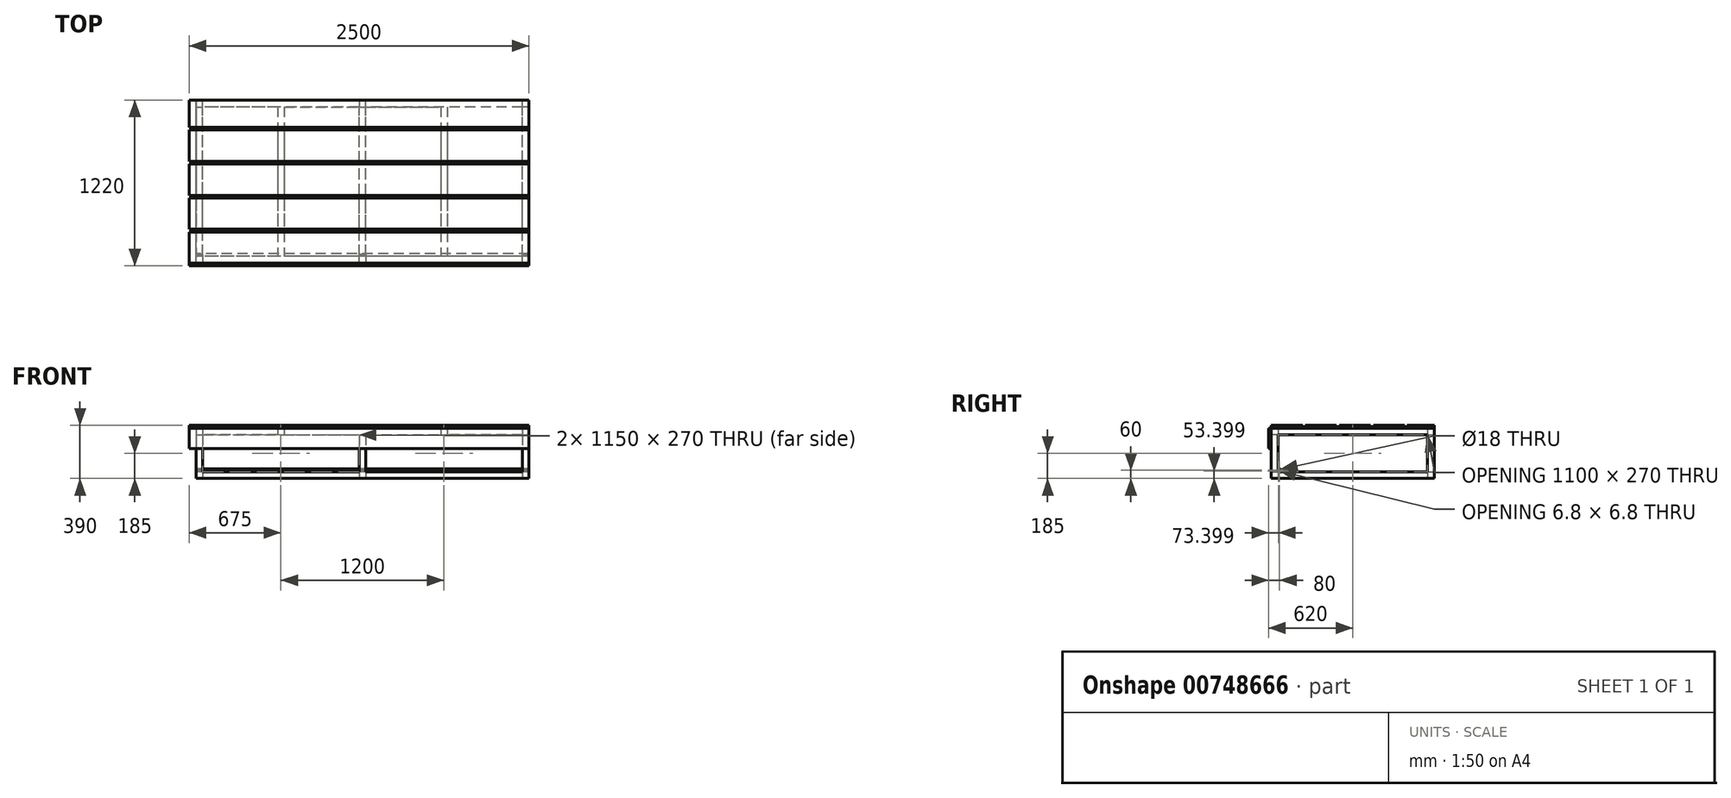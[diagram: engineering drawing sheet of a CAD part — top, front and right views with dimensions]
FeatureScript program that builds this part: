
annotation { "Feature Type Name" : "Feature", "Feature Type Description" : "" }
export const myFeature = defineFeature(function(context is Context, id is Id, definition is map)
    precondition{}
    {
        {
            var Q0;
            Q0=qCreatedBy(makeId("Top.planeOp"),FACE);
            var sketch = newSketch(context, id + "F0", { "sketchPlane" : qUnion([Q0])});
            skLineSegment(sketch, "E0.bottom", {"start": v(1225, -600) * mm, "end": v(-1225, -600) * mm});
            skLineSegment(sketch, "E0.top", {"start": v(1225, 600) * mm, "end": v(-1225, 600) * mm});
            skLineSegment(sketch, "E0.left", {"start": v(1225, -600) * mm, "end": v(1225, 600) * mm});
            skLineSegment(sketch, "E0.right", {"start": v(-1225, -600) * mm, "end": v(-1225, 600) * mm});
            skPoint(sketch, "E0.middle", {"position": v(0, 0) * mm});
            skLineSegment(sketch, "E1.0", {"start": v(1225, 550) * mm, "end": v(-1225, 550) * mm});
            skLineSegment(sketch, "E2.0", {"start": v(1227.5, -600) * mm, "end": v(1227.5, 600) * mm});
            skLineSegment(sketch, "E3.0", {"start": v(1175, -600) * mm, "end": v(1175, 600) * mm});
            skLineSegment(sketch, "E4.0", {"start": v(1225, -550) * mm, "end": v(-1225, -550) * mm});
            skLineSegment(sketch, "E5.0", {"start": v(-1175, -600) * mm, "end": v(-1175, 600) * mm});
            skLineSegment(sketch, "E6", {"start": v(0, 0) * mm, "end": v(0, 550) * mm});
            skLineSegment(sketch, "E7", {"start": v(0, 0) * mm, "end": v(0, -550) * mm});
            skLineSegment(sketch, "E8.0", {"start": v(25, 0) * mm, "end": v(25, 550) * mm});
            skLineSegment(sketch, "E9.0", {"start": v(-25, 0) * mm, "end": v(-25, 550) * mm});
            skLineSegment(sketch, "E10.0", {"start": v(-25, 0) * mm, "end": v(-25, -550) * mm});
            skLineSegment(sketch, "E11.0", {"start": v(25, 0) * mm, "end": v(25, -550) * mm});
            skSolve(sketch);
        }
        {
            var Q0;
            Q0 = qSketchRegion(id + "F0", true);
            var Q1;
            {var subQ1=sQuery(id+"F0.wireOp",EDGE,"E6");Q1=makeQuery(id+"F0.imprint","IMPRINT",FACE,{"disambiguationData":[TD([[makeQuery(id+"F0.imprint","IMPRINT",EDGE,{"derivedFrom":subQ1}),-1.0]])]});}
            var Q2;
            {var subQ3=sQuery(id+"F0.wireOp",EDGE,"E6");Q2=makeQuery(id+"F0.imprint","IMPRINT",FACE,{"disambiguationData":[TD([[makeQuery(id+"F0.imprint","IMPRINT",EDGE,{"derivedFrom":subQ3}),1.0]])]});}
            extrude(context, id + "F1", {"entities" : qUnion([Q0, Q1, Q2]), "depth" : 50 * mm, "offsetDistance" : 25 * mm});
        }
        {
            var Q0;
            Q0=makeQuery(id+"F1.opExtrude","CAP_FACE",FACE,{"disambiguationData":[OSD([sQuery(id+"F0.wireOp",EDGE,"E0.bottom"),sQuery(id+"F0.wireOp",EDGE,"E0.top"),sQuery(id+"F0.wireOp",EDGE,"E0.left"),sQuery(id+"F0.wireOp",EDGE,"E0.right"),sQuery(id+"F0.wireOp",EDGE,"E1.0"),sQuery(id+"F0.wireOp",EDGE,"E3.0"),sQuery(id+"F0.wireOp",EDGE,"E4.0"),sQuery(id+"F0.wireOp",EDGE,"E5.0"),sQuery(id+"F0.wireOp",EDGE,"E8.0"),sQuery(id+"F0.wireOp",EDGE,"E9.0"),sQuery(id+"F0.wireOp",EDGE,"E10.0"),sQuery(id+"F0.wireOp",EDGE,"E11.0")])],"isStart":false});
            var sketch = newSketch(context, id + "F2", { "sketchPlane" : qUnion([Q0])});
            skLineSegment(sketch, "E12", {"start": v(-25, 550) * mm, "end": v(25, 550) * mm});
            skLineSegment(sketch, "E13", {"start": v(25, 550) * mm, "end": v(25, 600) * mm});
            skLineSegment(sketch, "E14", {"start": v(25, 600) * mm, "end": v(-25, 600) * mm});
            skLineSegment(sketch, "E15", {"start": v(-25, 600) * mm, "end": v(-25, 550) * mm});
            skLineSegment(sketch, "E16", {"start": v(-1175, 550) * mm, "end": v(-1175, 600) * mm});
            skLineSegment(sketch, "E17", {"start": v(-1175, 600) * mm, "end": v(-1225, 600) * mm});
            skLineSegment(sketch, "E18", {"start": v(-1225, 600) * mm, "end": v(-1225, 550) * mm});
            skLineSegment(sketch, "E19", {"start": v(-1225, 550) * mm, "end": v(-1175, 550) * mm});
            skLineSegment(sketch, "E20", {"start": v(-1175, -550) * mm, "end": v(-1175, -600) * mm});
            skLineSegment(sketch, "E21", {"start": v(-1175, -600) * mm, "end": v(-1225, -600) * mm});
            skLineSegment(sketch, "E22", {"start": v(-1225, -600) * mm, "end": v(-1225, -550) * mm});
            skLineSegment(sketch, "E23", {"start": v(-1225, -550) * mm, "end": v(-1175, -550) * mm});
            skLineSegment(sketch, "E24", {"start": v(-25, -550) * mm, "end": v(25, -550) * mm});
            skLineSegment(sketch, "E25", {"start": v(25, -550) * mm, "end": v(25, -600) * mm});
            skLineSegment(sketch, "E26", {"start": v(25, -600) * mm, "end": v(-25, -600) * mm});
            skPoint(sketch, "E26.endSnap0", {"position": v(0, -600) * mm});
            skLineSegment(sketch, "E27", {"start": v(-25, -600) * mm, "end": v(-25, -550) * mm});
            skLineSegment(sketch, "E28", {"start": v(1175, -550) * mm, "end": v(1225, -550) * mm});
            skLineSegment(sketch, "E29", {"start": v(1225, -550) * mm, "end": v(1225, -600) * mm});
            skLineSegment(sketch, "E30", {"start": v(1225, -600) * mm, "end": v(1175, -600) * mm});
            skLineSegment(sketch, "E31", {"start": v(1175, -600) * mm, "end": v(1175, -550) * mm});
            skLineSegment(sketch, "E32", {"start": v(1175, 550) * mm, "end": v(1175, 600) * mm});
            skLineSegment(sketch, "E33", {"start": v(1175, 600) * mm, "end": v(1225, 600) * mm});
            skLineSegment(sketch, "E34", {"start": v(1225, 600) * mm, "end": v(1225, 550) * mm});
            skLineSegment(sketch, "E35", {"start": v(1225, 550) * mm, "end": v(1175, 550) * mm});
            skSolve(sketch);
        }
        {
            var Q0;
            Q0 = qSketchRegion(id + "F2", true);
            extrude(context, id + "F3", {"entities" : qUnion([Q0]), "operationType" : NewBodyOperationType.ADD, "depth" : 270 * mm, "offsetDistance" : 25 * mm});
        }
        {
            var Q0;
            Q0=makeQuery(id+"F3.opExtrude","CAP_FACE",FACE,{"disambiguationData":[OSD([sQuery(id+"F2.wireOp",EDGE,"E12"),sQuery(id+"F2.wireOp",EDGE,"E13"),sQuery(id+"F2.wireOp",EDGE,"E14"),sQuery(id+"F2.wireOp",EDGE,"E15")])],"isStart":false});
            var sketch = newSketch(context, id + "F4", { "sketchPlane" : qUnion([Q0])});
            skLineSegment(sketch, "E36.bottom", {"start": v(-1225, 600) * mm, "end": v(1225, 600) * mm});
            skLineSegment(sketch, "E36.top", {"start": v(-1225, -600) * mm, "end": v(1225, -600) * mm});
            skLineSegment(sketch, "E36.left", {"start": v(-1225, 600) * mm, "end": v(-1225, -600) * mm});
            skLineSegment(sketch, "E36.right", {"start": v(1225, 600) * mm, "end": v(1225, -600) * mm});
            skLineSegment(sketch, "E37.bottom", {"start": v(1175, -550) * mm, "end": v(-1175, -550) * mm});
            skLineSegment(sketch, "E37.top", {"start": v(1175, 550) * mm, "end": v(-1175, 550) * mm});
            skLineSegment(sketch, "E37.left", {"start": v(1175, -550) * mm, "end": v(1175, 550) * mm});
            skLineSegment(sketch, "E37.right", {"start": v(-1175, -550) * mm, "end": v(-1175, 550) * mm});
            skLineSegment(sketch, "E38.bottom", {"start": v(-25, 550) * mm, "end": v(25, 550) * mm});
            skLineSegment(sketch, "E38.top", {"start": v(-25, -550) * mm, "end": v(25, -550) * mm});
            skLineSegment(sketch, "E38.left", {"start": v(-25, 550) * mm, "end": v(-25, -550) * mm});
            skLineSegment(sketch, "E38.right", {"start": v(25, 550) * mm, "end": v(25, -550) * mm});
            skLineSegment(sketch, "E39", {"start": v(-25, 550) * mm, "end": v(-1175, 550) * mm});
            skLineSegment(sketch, "E40", {"start": v(-600, 550) * mm, "end": v(-600, -550) * mm});
            skLineSegment(sketch, "E41.0", {"start": v(-625, 550) * mm, "end": v(-625, -550) * mm});
            skLineSegment(sketch, "E42.0", {"start": v(-575, 550) * mm, "end": v(-575, -550) * mm});
            skLineSegment(sketch, "E43", {"start": v(25, 550) * mm, "end": v(1175, 550) * mm});
            skLineSegment(sketch, "E44", {"start": v(600, 550) * mm, "end": v(600, -550) * mm});
            skLineSegment(sketch, "E45.0", {"start": v(575, 550) * mm, "end": v(575, -550) * mm});
            skLineSegment(sketch, "E46.0", {"start": v(625, 550) * mm, "end": v(625, -550) * mm});
            skSolve(sketch);
        }
        {
            var Q0;
            Q0 = qSketchRegion(id + "F4", true);
            var Q1;
            {var subQ0=sQuery(id+"F4.wireOp",EDGE,"E40");Q1=makeQuery(id+"F4.imprint","IMPRINT",FACE,{"disambiguationData":[TD([[makeQuery(id+"F4.imprint","IMPRINT",EDGE,{"derivedFrom":subQ0}),1.0]])]});}
            var Q2;
            {var subQ0=sQuery(id+"F4.wireOp",EDGE,"E40");Q2=makeQuery(id+"F4.imprint","IMPRINT",FACE,{"disambiguationData":[TD([[makeQuery(id+"F4.imprint","IMPRINT",EDGE,{"derivedFrom":subQ0}),-1.0]])]});}
            var Q3;
            {var subQ0=sQuery(id+"F4.wireOp",EDGE,"E44");Q3=makeQuery(id+"F4.imprint","IMPRINT",FACE,{"disambiguationData":[TD([[makeQuery(id+"F4.imprint","IMPRINT",EDGE,{"derivedFrom":subQ0}),1.0]])]});}
            var Q4;
            {var subQ0=sQuery(id+"F4.wireOp",EDGE,"E44");Q4=makeQuery(id+"F4.imprint","IMPRINT",FACE,{"disambiguationData":[TD([[makeQuery(id+"F4.imprint","IMPRINT",EDGE,{"derivedFrom":subQ0}),-1.0]])]});}
            var Q5;
            Q5=makeQuery(id+"F4.imprint","IMPRINT",FACE,{"disambiguationData":[TD([[makeQuery(id+"F4.imprint","IMPRINT",EDGE,{"derivedFrom":sQuery(id+"F4.wireOp",EDGE,"E38.bottom")}),-1.0]])]});
            extrude(context, id + "F5", {"entities" : qUnion([Q0, Q1, Q2, Q3, Q4, Q5]), "operationType" : NewBodyOperationType.ADD, "depth" : 50 * mm, "offsetDistance" : 25 * mm});
        }
        {
            var Q0;
            Q0=makeQuery(id+"F5.boolean.opBoolean","MERGE",FACE,{"derivedFrom":[makeQuery(id+"F3.boolean.opBoolean","MERGE",FACE,{"derivedFrom":[makeQuery(id+"F1.opExtrude","SWEPT_FACE",FACE,{"disambiguationData":[OSD([sQuery(id+"F0.wireOp",EDGE,"E0.right")])]}),makeQuery(id+"F3.opExtrude","SWEPT_FACE",FACE,{"disambiguationData":[OSD([sQuery(id+"F2.wireOp",EDGE,"E18")])]}),makeQuery(id+"F3.opExtrude","SWEPT_FACE",FACE,{"disambiguationData":[OSD([sQuery(id+"F2.wireOp",EDGE,"E22")])]})]}),makeQuery(id+"F5.opExtrude","SWEPT_FACE",FACE,{"disambiguationData":[OSD([sQuery(id+"F4.wireOp",EDGE,"E36.left")])]})]});
            var sketch = newSketch(context, id + "F6", { "sketchPlane" : qUnion([Q0])});
            skLineSegment(sketch, "E47", {"start": v(550, 50) * mm, "end": v(550, 60) * mm});
            skLineSegment(sketch, "E48", {"start": v(550, 60) * mm, "end": v(540, 60) * mm});
            skCircle(sketch, "E49", {"center": v(540, 60) * mm, "radius": 10.5 * mm});
            skCircle(sketch, "E50", {"center": v(540, 60) * mm, "radius": 9 * mm});
            skSolve(sketch);
        }
        {
            var Q0;
            Q0 = qSketchRegion(id + "F6", true);
            extrude(context, id + "F7", {"entities" : qUnion([Q0]), "operationType" : NewBodyOperationType.ADD, "oppositeDirection" : true, "depth" : 2450 * mm, "offsetDistance" : 25 * mm});
        }
        {
            var Q0;
            Q0=makeQuery(id+"F5.boolean.opBoolean","MERGE",FACE,{"derivedFrom":[makeQuery(id+"F3.boolean.opBoolean","MERGE",FACE,{"derivedFrom":[makeQuery(id+"F1.opExtrude","SWEPT_FACE",FACE,{"disambiguationData":[OSD([sQuery(id+"F0.wireOp",EDGE,"E0.bottom")])]}),makeQuery(id+"F3.opExtrude","SWEPT_FACE",FACE,{"disambiguationData":[OSD([sQuery(id+"F2.wireOp",EDGE,"E21")])]}),makeQuery(id+"F3.opExtrude","SWEPT_FACE",FACE,{"disambiguationData":[OSD([sQuery(id+"F2.wireOp",EDGE,"E26")])]}),makeQuery(id+"F3.opExtrude","SWEPT_FACE",FACE,{"disambiguationData":[OSD([sQuery(id+"F2.wireOp",EDGE,"E30")])]})]}),makeQuery(id+"F5.opExtrude","SWEPT_FACE",FACE,{"disambiguationData":[OSD([sQuery(id+"F4.wireOp",EDGE,"E36.top")])]})]});
            var sketch = newSketch(context, id + "F8", { "sketchPlane" : qUnion([Q0])});
            skLineSegment(sketch, "E51.bottom", {"start": v(1225, 370) * mm, "end": v(-1275, 370) * mm});
            skLineSegment(sketch, "E51.top", {"start": v(1225, 220) * mm, "end": v(-1275, 220) * mm});
            skLineSegment(sketch, "E51.left", {"start": v(1225, 370) * mm, "end": v(1225, 220) * mm});
            skLineSegment(sketch, "E51.right", {"start": v(-1275, 370) * mm, "end": v(-1275, 220) * mm});
            skLineSegment(sketch, "E52", {"start": v(-1225, 370) * mm, "end": v(-1275, 370) * mm});
            skSolve(sketch);
        }
        {
            var Q0;
            Q0 = qSketchRegion(id + "F8", true);
            extrude(context, id + "F9", {"entities" : qUnion([Q0]), "depth" : 20 * mm, "offsetDistance" : 25 * mm});
        }
        {
            var Q0;
            Q0=makeQuery(id+"F5.opExtrude","CAP_FACE",FACE,{"disambiguationData":[OSD([sQuery(id+"F4.wireOp",EDGE,"E36.bottom"),sQuery(id+"F4.wireOp",EDGE,"E36.top"),sQuery(id+"F4.wireOp",EDGE,"E36.left"),sQuery(id+"F4.wireOp",EDGE,"E36.right"),sQuery(id+"F4.wireOp",EDGE,"E37.bottom"),sQuery(id+"F4.wireOp",EDGE,"E37.left"),sQuery(id+"F4.wireOp",EDGE,"E37.right"),sQuery(id+"F4.wireOp",EDGE,"E38.left"),sQuery(id+"F4.wireOp",EDGE,"E38.right"),sQuery(id+"F4.wireOp",EDGE,"E39"),sQuery(id+"F4.wireOp",EDGE,"E41.0"),sQuery(id+"F4.wireOp",EDGE,"E42.0"),sQuery(id+"F4.wireOp",EDGE,"E43"),sQuery(id+"F4.wireOp",EDGE,"E45.0"),sQuery(id+"F4.wireOp",EDGE,"E46.0")])],"isStart":false});
            var sketch = newSketch(context, id + "F10", { "sketchPlane" : qUnion([Q0])});
            skLineSegment(sketch, "E53.bottom", {"start": v(1225, 600) * mm, "end": v(-1275, 600) * mm});
            skLineSegment(sketch, "E53.top", {"start": v(1225, -600) * mm, "end": v(-1275, -600) * mm});
            skLineSegment(sketch, "E53.left", {"start": v(1225, 600) * mm, "end": v(1225, -600) * mm});
            skLineSegment(sketch, "E53.right", {"start": v(-1275, 600) * mm, "end": v(-1275, -600) * mm});
            skSolve(sketch);
        }
        {
            var Q0;
            Q0 = qSketchRegion(id + "F10", true);
            extrude(context, id + "F11", {"entities" : qUnion([Q0]), "depth" : 20 * mm, "offsetDistance" : 25 * mm});
        }
        {
            var Q0;
            Q0=makeQuery(id+"F11.opExtrude","SWEPT_FACE",FACE,{"disambiguationData":[OSD([sQuery(id+"F10.wireOp",EDGE,"E53.right")])]});
            var sketch = newSketch(context, id + "F12", { "sketchPlane" : qUnion([Q0])});
            skLineSegment(sketch, "E54", {"start": v(620, 370) * mm, "end": v(600, 370) * mm});
            skLineSegment(sketch, "E55", {"start": v(600, 370) * mm, "end": v(600, 390) * mm});
            skLineSegment(sketch, "E56", {"start": v(600, 390) * mm, "end": v(620, 390) * mm});
            skLineSegment(sketch, "E57", {"start": v(620, 390) * mm, "end": v(620, 370) * mm});
            skLineSegment(sketch, "E58.1.0.0", {"start": v(370, 390) * mm, "end": v(370, 370) * mm});
            skLineSegment(sketch, "E58.1.0.1", {"start": v(350, 390) * mm, "end": v(370, 390) * mm});
            skLineSegment(sketch, "E58.1.0.2", {"start": v(350, 370) * mm, "end": v(350, 390) * mm});
            skLineSegment(sketch, "E58.1.0.3", {"start": v(370, 370) * mm, "end": v(350, 370) * mm});
            skLineSegment(sketch, "E58.2.0.0", {"start": v(120, 390) * mm, "end": v(120, 370) * mm});
            skLineSegment(sketch, "E58.2.0.1", {"start": v(100, 390) * mm, "end": v(120, 390) * mm});
            skLineSegment(sketch, "E58.2.0.2", {"start": v(100, 370) * mm, "end": v(100, 390) * mm});
            skLineSegment(sketch, "E58.2.0.3", {"start": v(120, 370) * mm, "end": v(100, 370) * mm});
            skLineSegment(sketch, "E58.3.0.0", {"start": v(-130, 390) * mm, "end": v(-130, 370) * mm});
            skLineSegment(sketch, "E58.3.0.1", {"start": v(-150, 390) * mm, "end": v(-130, 390) * mm});
            skLineSegment(sketch, "E58.3.0.2", {"start": v(-150, 370) * mm, "end": v(-150, 390) * mm});
            skLineSegment(sketch, "E58.3.0.3", {"start": v(-130, 370) * mm, "end": v(-150, 370) * mm});
            skLineSegment(sketch, "E58.4.0.0", {"start": v(-380, 390) * mm, "end": v(-380, 370) * mm});
            skLineSegment(sketch, "E58.4.0.1", {"start": v(-400, 390) * mm, "end": v(-380, 390) * mm});
            skLineSegment(sketch, "E58.4.0.2", {"start": v(-400, 370) * mm, "end": v(-400, 390) * mm});
            skLineSegment(sketch, "E58.4.0.3", {"start": v(-380, 370) * mm, "end": v(-400, 370) * mm});
            skLineSegment(sketch, "E58.direction1", {"start": v(620, 370) * mm, "end": v(370, 370) * mm, "construction": true});
            skSolve(sketch);
        }
        {
            var Q0;
            Q0=makeQuery(id+"F12.imprint","IMPRINT",FACE,{"disambiguationData":[TD([[makeQuery(id+"F12.imprint","IMPRINT",EDGE,{"derivedFrom":sQuery(id+"F12.wireOp",EDGE,"E54")}),-1.0]])]});
            var Q1;
            Q1=makeQuery(id+"F12.imprint","IMPRINT",FACE,{"disambiguationData":[TD([[makeQuery(id+"F12.imprint","IMPRINT",EDGE,{"derivedFrom":sQuery(id+"F12.wireOp",EDGE,"E58.1.0.0")}),-1.0]])]});
            var Q2;
            Q2=makeQuery(id+"F12.imprint","IMPRINT",FACE,{"disambiguationData":[TD([[makeQuery(id+"F12.imprint","IMPRINT",EDGE,{"derivedFrom":sQuery(id+"F12.wireOp",EDGE,"E58.2.0.0")}),-1.0]])]});
            var Q3;
            Q3=makeQuery(id+"F12.imprint","IMPRINT",FACE,{"disambiguationData":[TD([[makeQuery(id+"F12.imprint","IMPRINT",EDGE,{"derivedFrom":sQuery(id+"F12.wireOp",EDGE,"E58.3.0.0")}),-1.0]])]});
            var Q4;
            Q4=makeQuery(id+"F12.imprint","IMPRINT",FACE,{"disambiguationData":[TD([[makeQuery(id+"F12.imprint","IMPRINT",EDGE,{"derivedFrom":sQuery(id+"F12.wireOp",EDGE,"E58.4.0.0")}),-1.0]])]});
            var Q5;
            Q5=makeQuery(id+"F11.opExtrude","SWEPT_FACE",FACE,{"disambiguationData":[OSD([sQuery(id+"F10.wireOp",EDGE,"E53.left")])]});
            extrude(context, id + "F13", {"entities" : qUnion([Q0, Q1, Q2, Q3, Q4]), "operationType" : NewBodyOperationType.REMOVE, "endBound" : BoundingType.UP_TO_SURFACE, "oppositeDirection" : true, "depth" : 25 * mm, "endBoundEntityFace" : qUnion([Q5]), "offsetDistance" : 25 * mm});
        }
    });
